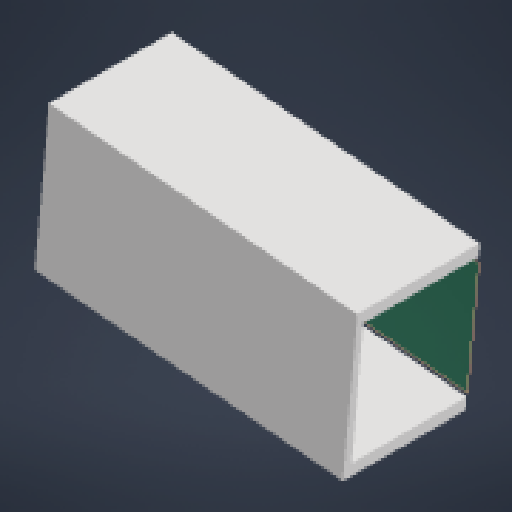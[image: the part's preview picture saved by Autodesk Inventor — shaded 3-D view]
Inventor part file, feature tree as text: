
AUTODESK INVENTOR PART (.ipt)
format: ipt  version: 2024.2 (Build 282272000, 272)  size: 159,232 bytes
history: native  units: in
note: dims shown in document units (in); Inventor stores cm internally (conversion verified against a paired STEP export)
features: extrude x2, sketch x2, other x2, plane x1, fillet x1
ambient origin geometry x8: Origin, YZ Plane, XZ Plane, XY Plane, X Axis, Y Axis, Z Axis, Center Point
bodies: Solid1 (feature_tree)
feature tree (8):
  plane  "Work Plane1"
  extrude  "Extrusion1"  Depth=2.0472in
  extrude  "Extrusion2"  Depth=0.0625in
  fillet  "Fillet1"  Radius=0.1969in
  sketch  "Sketch1"  dims[d0=4.5669in d1=2.0472in]
  sketch  "Sketch2"  dims[d2=0.0984in d3=0.1575in d4=0.1969in d5=1.8504in d6=0.0in d7=0.1181in d8=0.0in d9=0.0625in]
  other  "Assembly1"
  other  "Matrix 12V 3000mAh NiMH Battery 14-0014 - Matrix 12V 3000mAh NiMH Battery 14-0014:1"
